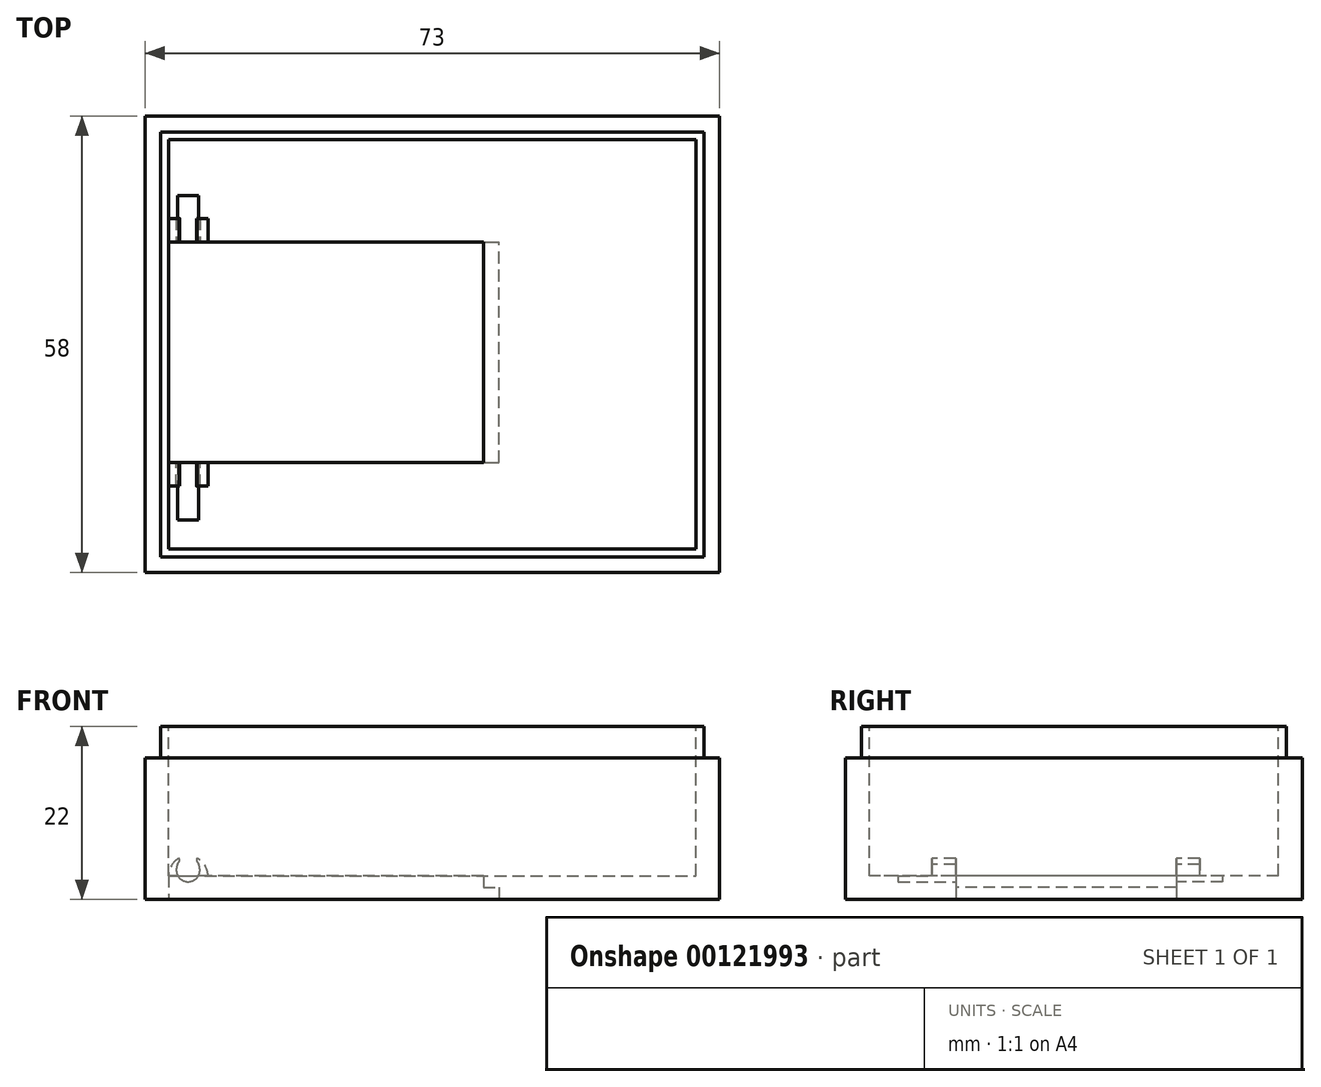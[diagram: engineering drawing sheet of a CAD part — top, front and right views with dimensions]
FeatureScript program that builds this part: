
annotation { "Feature Type Name" : "Feature", "Feature Type Description" : "" }
export const myFeature = defineFeature(function(context is Context, id is Id, definition is map)
    precondition{}
    {
        {
            var Q0;
            Q0=qCreatedBy(makeId("Front.planeOp"),FACE);
            var sketch = newSketch(context, id + "F0", { "sketchPlane" : qUnion([Q0])});
            skLineSegment(sketch, "E0.bottom", {"start": v(36.5, -11) * mm, "end": v(-36.5, -11) * mm});
            skLineSegment(sketch, "E0.top", {"start": v(36.5, 11) * mm, "end": v(-36.5, 11) * mm});
            skLineSegment(sketch, "E0.left", {"start": v(36.5, -11) * mm, "end": v(36.5, 11) * mm});
            skLineSegment(sketch, "E0.right", {"start": v(-36.5, -11) * mm, "end": v(-36.5, 11) * mm});
            skPoint(sketch, "E0.middle", {"position": v(0, 0) * mm});
            skFitSpline(sketch, "E1", {"points": [v(-0.93, -0.38) * mm, v(-0.75, 0.37) * mm], "startDerivative": vector(0.3, 0.98) * mm, "endDerivative": vector(-0.8, 0.77) * mm});
            skFitSpline(sketch, "E2", {"points": [v(0.91, -0.38) * mm, v(0.8, 0.37) * mm], "startDerivative": vector(-0.3, 0.98) * mm, "endDerivative": vector(1, 0.77) * mm});
            skSolve(sketch);
        }
        {
            var Q0;
            Q0=makeQuery(id+"F0.imprint","IMPRINT",FACE,{"disambiguationData":[TD([[makeQuery(id+"F0.imprint","IMPRINT",EDGE,{"derivedFrom":sQuery(id+"F0.wireOp",EDGE,"E0.bottom")}),-1.0]])]});
            extrude(context, id + "F1", {"entities" : qUnion([Q0]), "depth" : 58 * mm, "symmetric" : true});
        }
        {
            var Q0;
            Q0=makeQuery(id+"F1.opExtrude","SWEPT_FACE",FACE,{"disambiguationData":[OSD([sQuery(id+"F0.wireOp",EDGE,"E0.top")])]});
            var sketch = newSketch(context, id + "F2", { "sketchPlane" : qUnion([Q0])});
            skLineSegment(sketch, "E3.bottom", {"start": v(-33.5, 26) * mm, "end": v(33.5, 26) * mm});
            skLineSegment(sketch, "E3.top", {"start": v(-33.5, -26) * mm, "end": v(33.5, -26) * mm});
            skLineSegment(sketch, "E3.left", {"start": v(-33.5, 26) * mm, "end": v(-33.5, -26) * mm});
            skLineSegment(sketch, "E3.right", {"start": v(33.5, 26) * mm, "end": v(33.5, -26) * mm});
            skPoint(sketch, "E3.middle", {"position": v(0, 0) * mm});
            skSolve(sketch);
        }
        {
            var Q0;
            Q0 = qSketchRegion(id + "F2", true);
            extrude(context, id + "F3", {"entities" : qUnion([Q0]), "operationType" : NewBodyOperationType.REMOVE, "oppositeDirection" : true, "depth" : 19 * mm});
        }
        {
            var Q0;
            Q0=makeQuery(id+"F1.opExtrude","SWEPT_FACE",FACE,{"disambiguationData":[OSD([sQuery(id+"F0.wireOp",EDGE,"E0.left")])]});
            var sketch = newSketch(context, id + "F4", { "sketchPlane" : qUnion([Q0])});
            skLineSegment(sketch, "E4.bottom", {"start": v(-29, 11) * mm, "end": v(29, 11) * mm});
            skLineSegment(sketch, "E4.top", {"start": v(-29, 7) * mm, "end": v(29, 7) * mm});
            skLineSegment(sketch, "E4.left", {"start": v(-29, 11) * mm, "end": v(-29, 7) * mm});
            skLineSegment(sketch, "E4.right", {"start": v(29, 11) * mm, "end": v(29, 7) * mm});
            skSolve(sketch);
        }
        {
            var Q0;
            Q0 = qSketchRegion(id + "F4", true);
            extrude(context, id + "F5", {"entities" : qUnion([Q0]), "operationType" : NewBodyOperationType.REMOVE, "oppositeDirection" : true, "depth" : 2 * mm});
        }
        {
            var Q0;
            Q0=makeQuery(id+"F1.opExtrude","CAP_FACE",FACE,{"disambiguationData":[OSD([sQuery(id+"F0.wireOp",EDGE,"E0.bottom"),sQuery(id+"F0.wireOp",EDGE,"E0.top"),sQuery(id+"F0.wireOp",EDGE,"E0.left"),sQuery(id+"F0.wireOp",EDGE,"E0.right")])],"isStart":false});
            var sketch = newSketch(context, id + "F6", { "sketchPlane" : qUnion([Q0])});
            skLineSegment(sketch, "E5.bottom", {"start": v(-36.5, 11) * mm, "end": v(34.5, 11) * mm});
            skLineSegment(sketch, "E5.top", {"start": v(-36.5, 7) * mm, "end": v(34.5, 7) * mm});
            skLineSegment(sketch, "E5.left", {"start": v(-36.5, 11) * mm, "end": v(-36.5, 7) * mm});
            skLineSegment(sketch, "E5.right", {"start": v(34.5, 11) * mm, "end": v(34.5, 7) * mm});
            skSolve(sketch);
        }
        {
            var Q0;
            Q0 = qSketchRegion(id + "F6", true);
            extrude(context, id + "F7", {"entities" : qUnion([Q0]), "operationType" : NewBodyOperationType.REMOVE, "flatOperationType" : FlatOperationType.REMOVE, "oppositeDirection" : true, "offsetDistance" : 25 * mm, "depth" : 2 * mm, "domain" : OperationDomain.MODEL});
        }
        {
            var Q0;
            Q0=makeQuery(id+"F1.opExtrude","SWEPT_FACE",FACE,{"disambiguationData":[OSD([sQuery(id+"F0.wireOp",EDGE,"E0.right")])]});
            var sketch = newSketch(context, id + "F8", { "sketchPlane" : qUnion([Q0])});
            skLineSegment(sketch, "E6.bottom", {"start": v(-29, 11) * mm, "end": v(27, 11) * mm});
            skLineSegment(sketch, "E6.top", {"start": v(-29, 7) * mm, "end": v(27, 7) * mm});
            skLineSegment(sketch, "E6.left", {"start": v(-29, 11) * mm, "end": v(-29, 7) * mm});
            skLineSegment(sketch, "E6.right", {"start": v(27, 11) * mm, "end": v(27, 7) * mm});
            skSolve(sketch);
        }
        {
            var Q0;
            Q0 = qSketchRegion(id + "F8", true);
            extrude(context, id + "F9", {"entities" : qUnion([Q0]), "operationType" : NewBodyOperationType.REMOVE, "oppositeDirection" : true, "depth" : 2 * mm});
        }
        {
            var Q0;
            Q0=makeQuery(id+"F1.opExtrude","CAP_FACE",FACE,{"disambiguationData":[OSD([sQuery(id+"F0.wireOp",EDGE,"E0.bottom"),sQuery(id+"F0.wireOp",EDGE,"E0.top"),sQuery(id+"F0.wireOp",EDGE,"E0.left"),sQuery(id+"F0.wireOp",EDGE,"E0.right")])],"isStart":true});
            var sketch = newSketch(context, id + "F10", { "sketchPlane" : qUnion([Q0])});
            skLineSegment(sketch, "E7.bottom", {"start": v(-34.5, 11) * mm, "end": v(34.5, 11) * mm});
            skLineSegment(sketch, "E7.top", {"start": v(-34.5, 7) * mm, "end": v(34.5, 7) * mm});
            skLineSegment(sketch, "E7.left", {"start": v(-34.5, 11) * mm, "end": v(-34.5, 7) * mm});
            skLineSegment(sketch, "E7.right", {"start": v(34.5, 11) * mm, "end": v(34.5, 7) * mm});
            skSolve(sketch);
        }
        {
            var Q0;
            Q0 = qSketchRegion(id + "F10", true);
            extrude(context, id + "F11", {"entities" : qUnion([Q0]), "operationType" : NewBodyOperationType.REMOVE, "oppositeDirection" : true, "depth" : 2 * mm});
        }
        {
            var Q0;
            Q0=makeQuery(id+"F1.opExtrude","SWEPT_FACE",FACE,{"disambiguationData":[OSD([sQuery(id+"F0.wireOp",EDGE,"E0.bottom")])]});
            var sketch = newSketch(context, id + "F12", { "sketchPlane" : qUnion([Q0])});
            skLineSegment(sketch, "E8.bottom", {"start": v(-33.5, 15) * mm, "end": v(8.5, 15) * mm});
            skLineSegment(sketch, "E8.top", {"start": v(-33.5, -13) * mm, "end": v(8.5, -13) * mm});
            skLineSegment(sketch, "E8.left", {"start": v(-33.5, 15) * mm, "end": v(-33.5, -13) * mm});
            skLineSegment(sketch, "E8.right", {"start": v(8.5, 15) * mm, "end": v(8.5, -13) * mm});
            skSolve(sketch);
        }
        {
            var Q0;
            Q0 = qSketchRegion(id + "F12", true);
            extrude(context, id + "F13", {"entities" : qUnion([Q0]), "operationType" : NewBodyOperationType.REMOVE, "endBound" : BoundingType.THROUGH_ALL, "oppositeDirection" : true, "depth" : 25 * mm});
        }
        {
            var Q0;
            Q0=makeQuery(id+"F3.boolean.opBoolean","COPY",FACE,{"derivedFrom":makeQuery(id+"F3.opExtrude","CAP_FACE",FACE,{"disambiguationData":[OSD([sQuery(id+"F2.wireOp",EDGE,"E3.bottom"),sQuery(id+"F2.wireOp",EDGE,"E3.top"),sQuery(id+"F2.wireOp",EDGE,"E3.left"),sQuery(id+"F2.wireOp",EDGE,"E3.right")])],"isStart":false})});
            var sketch = newSketch(context, id + "F14", { "sketchPlane" : qUnion([Q0])});
            skLineSegment(sketch, "E9.bottom", {"start": v(-33.5, -15) * mm, "end": v(-31, -15) * mm});
            skLineSegment(sketch, "E9.top", {"start": v(-33.5, -18) * mm, "end": v(-31, -18) * mm});
            skLineSegment(sketch, "E9.left", {"start": v(-33.5, -15) * mm, "end": v(-33.5, -18) * mm});
            skLineSegment(sketch, "E9.right", {"start": v(-31, -15) * mm, "end": v(-31, -18) * mm});
            skSolve(sketch);
        }
        {
            var Q0;
            Q0 = qSketchRegion(id + "F14", true);
            var Q1;
            Q1=sQuery(id+"F14.wireOp",EDGE,"E9.right");
            revolve(context, id + "F15", {"operationType" : NewBodyOperationType.ADD, "entities" : qUnion([Q0]), "axis" : qUnion([Q1]), "revolveType" : RevolveType.ONE_DIRECTION, "oppositeDirection" : true, "angle" : 360 * degree});
        }
        {
            var Q0;
            Q0=makeQuery(id+"F3.boolean.opBoolean","COPY",FACE,{"derivedFrom":makeQuery(id+"F3.opExtrude","CAP_FACE",FACE,{"disambiguationData":[OSD([sQuery(id+"F2.wireOp",EDGE,"E3.bottom"),sQuery(id+"F2.wireOp",EDGE,"E3.top"),sQuery(id+"F2.wireOp",EDGE,"E3.left"),sQuery(id+"F2.wireOp",EDGE,"E3.right")])],"isStart":false})});
            var sketch = newSketch(context, id + "F16", { "sketchPlane" : qUnion([Q0])});
            skLineSegment(sketch, "E10.bottom", {"start": v(-33.5, 13) * mm, "end": v(-31, 13) * mm});
            skLineSegment(sketch, "E10.top", {"start": v(-33.5, 16) * mm, "end": v(-31, 16) * mm});
            skLineSegment(sketch, "E10.left", {"start": v(-33.5, 13) * mm, "end": v(-33.5, 16) * mm});
            skLineSegment(sketch, "E10.right", {"start": v(-31, 13) * mm, "end": v(-31, 16) * mm});
            skSolve(sketch);
        }
        {
            var Q0;
            Q0 = qSketchRegion(id + "F16", true);
            var Q1;
            Q1=sQuery(id+"F16.wireOp",EDGE,"E10.right");
            revolve(context, id + "F17", {"operationType" : NewBodyOperationType.ADD, "entities" : qUnion([Q0]), "axis" : qUnion([Q1]), "revolveType" : RevolveType.FULL});
        }
        {
            var Q0;
            Q0=makeQuery(id+"F17.boolean.opBoolean","MERGE",FACE,{"derivedFrom":[makeQuery(id+"F13.boolean.opBoolean","COPY",FACE,{"derivedFrom":makeQuery(id+"F13.opExtrude","SWEPT_FACE",FACE,{"disambiguationData":[OSD([sQuery(id+"F12.wireOp",EDGE,"E8.top")])]})}),makeQuery(id+"F17.opRevolve","SWEPT_FACE",FACE,{"disambiguationData":[OSD([sQuery(id+"F16.wireOp",EDGE,"E10.bottom")])]})]});
            var sketch = newSketch(context, id + "F18", { "sketchPlane" : qUnion([Q0])});
            skCircle(sketch, "E11", {"center": v(-31.02, -7.26) * mm, "radius": 1.5 * mm});
            skSolve(sketch);
        }
        {
            var Q0;
            Q0 = qSketchRegion(id + "F18", true);
            extrude(context, id + "F19", {"entities" : qUnion([Q0]), "operationType" : NewBodyOperationType.REMOVE, "depth" : 35.33 * mm});
        }
        {
            var Q0;
            Q0 = qSketchRegion(id + "F18", true);
            extrude(context, id + "F20", {"entities" : qUnion([Q0]), "operationType" : NewBodyOperationType.REMOVE, "oppositeDirection" : true, "depth" : 5.88 * mm});
        }
        {
            var Q0;
            Q0=makeQuery(id+"F15.opRevolve","SWEPT_FACE",FACE,{"disambiguationData":[OSD([sQuery(id+"F14.wireOp",EDGE,"E9.top")])]});
            var sketch = newSketch(context, id + "F21", { "sketchPlane" : qUnion([Q0])});
            skFitSpline(sketch, "E12", {"points": [v(-32.36, -6.58) * mm, v(-32.18, -5.8) * mm], "startDerivative": vector(0.27, 1) * mm, "endDerivative": vector(-0.8, 0.77) * mm});
            skFitSpline(sketch, "E13", {"points": [v(-29.85, -5.78) * mm, v(-29.68, -6.58) * mm], "startDerivative": vector(-0.84, -0.82) * mm, "endDerivative": vector(0.31, -1) * mm});
            skSolve(sketch);
        }
        {
            var Q0;
            {var subQ0=sQuery(id+"F21.wireOp",EDGE,"E12");Q0=makeQuery(id+"F21.imprint","IMPRINT",FACE,{"disambiguationData":[TD([[makeQuery(id+"F21.imprint","IMPRINT",EDGE,{"derivedFrom":subQ0}),-1.0]])]});}
            extrude(context, id + "F22", {"entities" : qUnion([Q0]), "operationType" : NewBodyOperationType.REMOVE, "oppositeDirection" : true, "depth" : 38.63 * mm});
        }
        {
            var Q0;
            Q0=makeQuery(id+"F13.boolean.opBoolean","COPY",FACE,{"derivedFrom":makeQuery(id+"F13.opExtrude","SWEPT_FACE",FACE,{"disambiguationData":[OSD([sQuery(id+"F12.wireOp",EDGE,"E8.right")])]})});
            var sketch = newSketch(context, id + "F23", { "sketchPlane" : qUnion([Q0])});
            skLineSegment(sketch, "E14.bottom", {"start": v(-13, -8) * mm, "end": v(15, -8) * mm});
            skLineSegment(sketch, "E14.top", {"start": v(-13, -9.5) * mm, "end": v(15, -9.5) * mm});
            skLineSegment(sketch, "E14.left", {"start": v(-13, -8) * mm, "end": v(-13, -9.5) * mm});
            skLineSegment(sketch, "E14.right", {"start": v(15, -8) * mm, "end": v(15, -9.5) * mm});
            skSolve(sketch);
        }
        {
            var Q0;
            Q0 = qSketchRegion(id + "F23", true);
            extrude(context, id + "F24", {"entities" : qUnion([Q0]), "operationType" : NewBodyOperationType.ADD, "depth" : 2 * mm});
        }
    });
